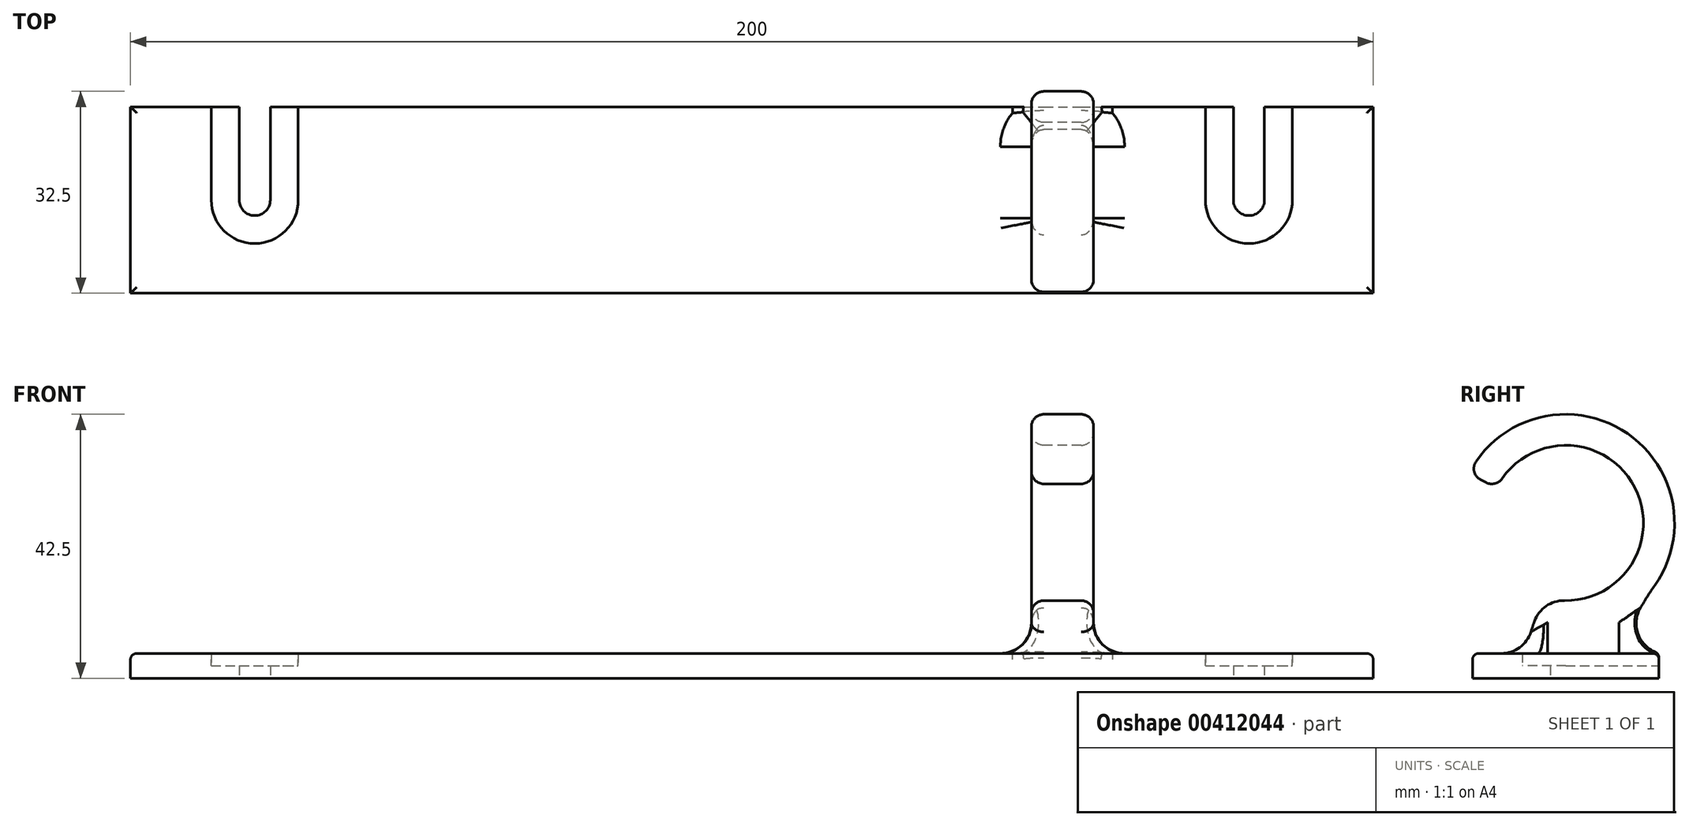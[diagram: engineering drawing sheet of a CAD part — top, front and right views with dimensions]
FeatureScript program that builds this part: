
annotation { "Feature Type Name" : "Feature", "Feature Type Description" : "" }
export const myFeature = defineFeature(function(context is Context, id is Id, definition is map)
    precondition{}
    {
        {
            var Q0;
            Q0=qCreatedBy(makeId("Top.planeOp"),FACE);
            var sketch = newSketch(context, id + "F0", { "sketchPlane" : qUnion([Q0])});
            skLineSegment(sketch, "E0.bottom", {"start": v(-100, 15) * mm, "end": v(-82.5, 15) * mm});
            skLineSegment(sketch, "E0.top", {"start": v(-100, -15) * mm, "end": v(100, -15) * mm});
            skLineSegment(sketch, "E0.left", {"start": v(-100, 15) * mm, "end": v(-100, -15) * mm});
            skLineSegment(sketch, "E0.right", {"start": v(100, 15) * mm, "end": v(100, -15) * mm});
            skCircle(sketch, "E1", {"center": v(-223.53, 13.27) * mm, "radius": 2.5 * mm});
            skArc(sketch, "E2", {"start": v(-82.5, 0) * mm, "mid": v(-80, -2.5) * mm, "end": v(-77.5, 0) * mm});
            skArc(sketch, "E3", {"start": v(77.5, 0) * mm, "mid": v(80, -2.5) * mm, "end": v(82.5, 0) * mm});
            skLineSegment(sketch, "E4", {"start": v(-82.5, 0) * mm, "end": v(-82.5, 15) * mm});
            skLineSegment(sketch, "E5", {"start": v(-77.5, 0) * mm, "end": v(-77.5, 15) * mm});
            skLineSegment(sketch, "E6", {"start": v(77.5, 0) * mm, "end": v(77.5, 15) * mm});
            skLineSegment(sketch, "E7", {"start": v(82.5, 0) * mm, "end": v(82.5, 15) * mm});
            skLineSegment(sketch, "E8.trimOffspring", {"start": v(-77.5, 15) * mm, "end": v(77.5, 15) * mm});
            skLineSegment(sketch, "E9.trimOffspring", {"start": v(82.5, 15) * mm, "end": v(100, 15) * mm});
            skSolve(sketch);
        }
        {
            var Q0;
            Q0=makeQuery(id+"F0.imprint","IMPRINT",FACE,{"disambiguationData":[TD([[makeQuery(id+"F0.imprint","IMPRINT",EDGE,{"derivedFrom":sQuery(id+"F0.wireOp",EDGE,"E0.bottom")}),-1.0]])]});
            var sketch = newSketch(context, id + "F1", { "sketchPlane" : qUnion([Q0])});
            skArc(sketch, "E10", {"start": v(-87, 0) * mm, "mid": v(-80, -7) * mm, "end": v(-73, 0) * mm});
            skArc(sketch, "E11", {"start": v(73, 0) * mm, "mid": v(80, -7) * mm, "end": v(87, 0) * mm});
            skLineSegment(sketch, "E12", {"start": v(-73, 0) * mm, "end": v(-73, 24.4) * mm});
            skLineSegment(sketch, "E13", {"start": v(-87, 0) * mm, "end": v(-87, 24.4) * mm});
            skLineSegment(sketch, "E14", {"start": v(-87, 24.4) * mm, "end": v(-73, 24.4) * mm});
            skLineSegment(sketch, "E15", {"start": v(73, 0) * mm, "end": v(73, 21.79) * mm});
            skLineSegment(sketch, "E16", {"start": v(87, 0) * mm, "end": v(87, 21.79) * mm});
            skLineSegment(sketch, "E17", {"start": v(87, 21.79) * mm, "end": v(73, 21.79) * mm});
            skSolve(sketch);
        }
        {
            var Q0;
            Q0 = qSketchRegion(id + "F0", true);
            extrude(context, id + "F2", {"entities" : qUnion([Q0]), "depth" : 4 * mm});
        }
        {
            var Q0;
            Q0 = qSketchRegion(id + "F1", true);
            extrude(context, id + "F3", {"entities" : qUnion([Q0]), "operationType" : NewBodyOperationType.REMOVE, "depth" : 25 * mm, "hasSecondDirection" : true, "secondDirectionOppositeDirection" : false, "secondDirectionDepth" : 2 * mm});
        }
        {
            var Q0;
            Q0=qCreatedBy(makeId("Right.planeOp"),FACE);
            var sketch = newSketch(context, id + "F4", { "sketchPlane" : qUnion([Q0])});
            skArc(sketch, "E18", {"start": v(14.32, 14.95) * mm, "mid": v(9.97, 39.39) * mm, "end": v(-14.45, 34.88) * mm});
            skArc(sketch, "E19", {"start": v(-0.22, 12.5) * mm, "mid": v(11.13, 30.68) * mm, "end": v(-10.25, 32.15) * mm});
            skLineSegment(sketch, "E20", {"start": v(-12.8, 31.5) * mm, "end": v(-13.7, 31.97) * mm});
            skLineSegment(sketch, "E21", {"start": v(-7.5, 0) * mm, "end": v(7.5, 0) * mm});
            skArc(sketch, "E22", {"start": v(14.32, 14.95) * mm, "mid": v(10.22, 7.79) * mm, "end": v(7.5, 0) * mm});
            skArc(sketch, "E23.trimOffspring", {"start": v(-5.02, 9.19) * mm, "mid": v(-6.44, 4.64) * mm, "end": v(-7.5, 0) * mm});
            skPoint(sketch, "E24.visualSharp", {"position": v(-3.5, 13) * mm});
            skArc(sketch, "E24.filletArc", {"start": v(-0.22, 12.5) * mm, "mid": v(-3.16, 11.62) * mm, "end": v(-5.02, 9.19) * mm});
            skPoint(sketch, "E25.visualSharp", {"position": v(-11.14, 30.67) * mm});
            skArc(sketch, "E25.filletArc", {"start": v(-12.8, 31.5) * mm, "mid": v(-11.4, 31.35) * mm, "end": v(-10.25, 32.15) * mm});
            skPoint(sketch, "E26.visualSharp", {"position": v(-15.6, 32.93) * mm});
            skArc(sketch, "E26.filletArc", {"start": v(-14.45, 34.88) * mm, "mid": v(-14.73, 33.25) * mm, "end": v(-13.7, 31.97) * mm});
            skSolve(sketch);
        }
        {
            var Q0;
            Q0 = qSketchRegion(id + "F4", true);
            extrude(context, id + "F5", {"entities" : qUnion([Q0]), "operationType" : NewBodyOperationType.ADD, "depth" : 55 * mm, "hasSecondDirection" : true, "secondDirectionOppositeDirection" : false, "secondDirectionDepth" : 45 * mm});
        }
        {
            var Q0;
            Q0=makeQuery(id+"F5.opExtrude","CAP_EDGE",EDGE,{"disambiguationData":[OSD([sQuery(id+"F4.wireOp",EDGE,"E18")])],"isStart":false});
            var Q1;
            Q1=makeQuery(id+"F5.opExtrude","CAP_EDGE",EDGE,{"disambiguationData":[OSD([sQuery(id+"F4.wireOp",EDGE,"E19")])],"isStart":false});
            var Q2;
            Q2=makeQuery(id+"F5.opExtrude","CAP_EDGE",EDGE,{"disambiguationData":[OSD([sQuery(id+"F4.wireOp",EDGE,"E22")])],"isStart":false});
            var Q3;
            Q3=makeQuery(id+"F5.opExtrude","CAP_EDGE",EDGE,{"disambiguationData":[OSD([sQuery(id+"F4.wireOp",EDGE,"E23.trimOffspring")])],"isStart":false});
            var Q4;
            Q4=makeQuery(id+"F5.opExtrude","CAP_EDGE",EDGE,{"disambiguationData":[OSD([sQuery(id+"F4.wireOp",EDGE,"E18")])],"isStart":true});
            var Q5;
            Q5=makeQuery(id+"F5.opExtrude","CAP_EDGE",EDGE,{"disambiguationData":[OSD([sQuery(id+"F4.wireOp",EDGE,"E22")])],"isStart":true});
            fillet(context, id + "F6", {"entities" : qUnion([Q0, Q1, Q2, Q3, Q4, Q5]), "radius" : 2 * mm, "tangentPropagation" : true, "allowEdgeOverflow" : false});
        }
        {
            var Q0;
            Q0=makeQuery(id+"F2.opExtrude","SWEPT_BODY",BODY,{"disambiguationData":[OSD([sQuery(id+"F0.wireOp",EDGE,"E1")])]});
            deleteBodies(context, id + "F7", {"entities" : qUnion([Q0])});
        }
        {
            var Q0;
            Q0=makeQuery(id+"F5.opExtrude","CAP_FACE",FACE,{"disambiguationData":[OSD([sQuery(id+"F4.wireOp",EDGE,"E18"),sQuery(id+"F4.wireOp",EDGE,"E19"),sQuery(id+"F4.wireOp",EDGE,"E20"),sQuery(id+"F4.wireOp",EDGE,"E21"),sQuery(id+"F4.wireOp",EDGE,"E22"),sQuery(id+"F4.wireOp",EDGE,"E23.trimOffspring"),sQuery(id+"F4.wireOp",EDGE,"E24.filletArc"),sQuery(id+"F4.wireOp",EDGE,"E25.filletArc"),sQuery(id+"F4.wireOp",EDGE,"E26.filletArc")])],"isStart":false});
            fillet(context, id + "F8", {"entities" : qUnion([Q0]), "radius" : 5 * mm, "tangentPropagation" : true, "allowEdgeOverflow" : false});
        }
        {
            var Q0;
            Q0=makeQuery(id+"F2.opExtrude","CAP_EDGE",EDGE,{"disambiguationData":[OSD([sQuery(id+"F0.wireOp",EDGE,"E8.trimOffspring")])],"isStart":false});
            var Q1;
            Q1=makeQuery(id+"F2.opExtrude","CAP_EDGE",EDGE,{"disambiguationData":[OSD([sQuery(id+"F0.wireOp",EDGE,"E0.bottom")])],"isStart":false});
            var Q2;
            Q2=makeQuery(id+"F2.opExtrude","CAP_EDGE",EDGE,{"disambiguationData":[OSD([sQuery(id+"F0.wireOp",EDGE,"E0.left")])],"isStart":false});
            var Q3;
            Q3=makeQuery(id+"F2.opExtrude","CAP_EDGE",EDGE,{"disambiguationData":[OSD([sQuery(id+"F0.wireOp",EDGE,"E0.top")])],"isStart":false});
            var Q4;
            Q4=makeQuery(id+"F2.opExtrude","CAP_EDGE",EDGE,{"disambiguationData":[OSD([sQuery(id+"F0.wireOp",EDGE,"E0.right")])],"isStart":false});
            var Q5;
            Q5=makeQuery(id+"F2.opExtrude","CAP_EDGE",EDGE,{"disambiguationData":[OSD([sQuery(id+"F0.wireOp",EDGE,"E9.trimOffspring")])],"isStart":false});
            fillet(context, id + "F9", {"entities" : qUnion([Q0, Q1, Q2, Q3, Q4, Q5]), "radius" : 1 * mm, "tangentPropagation" : true, "allowEdgeOverflow" : false});
        }
    });
